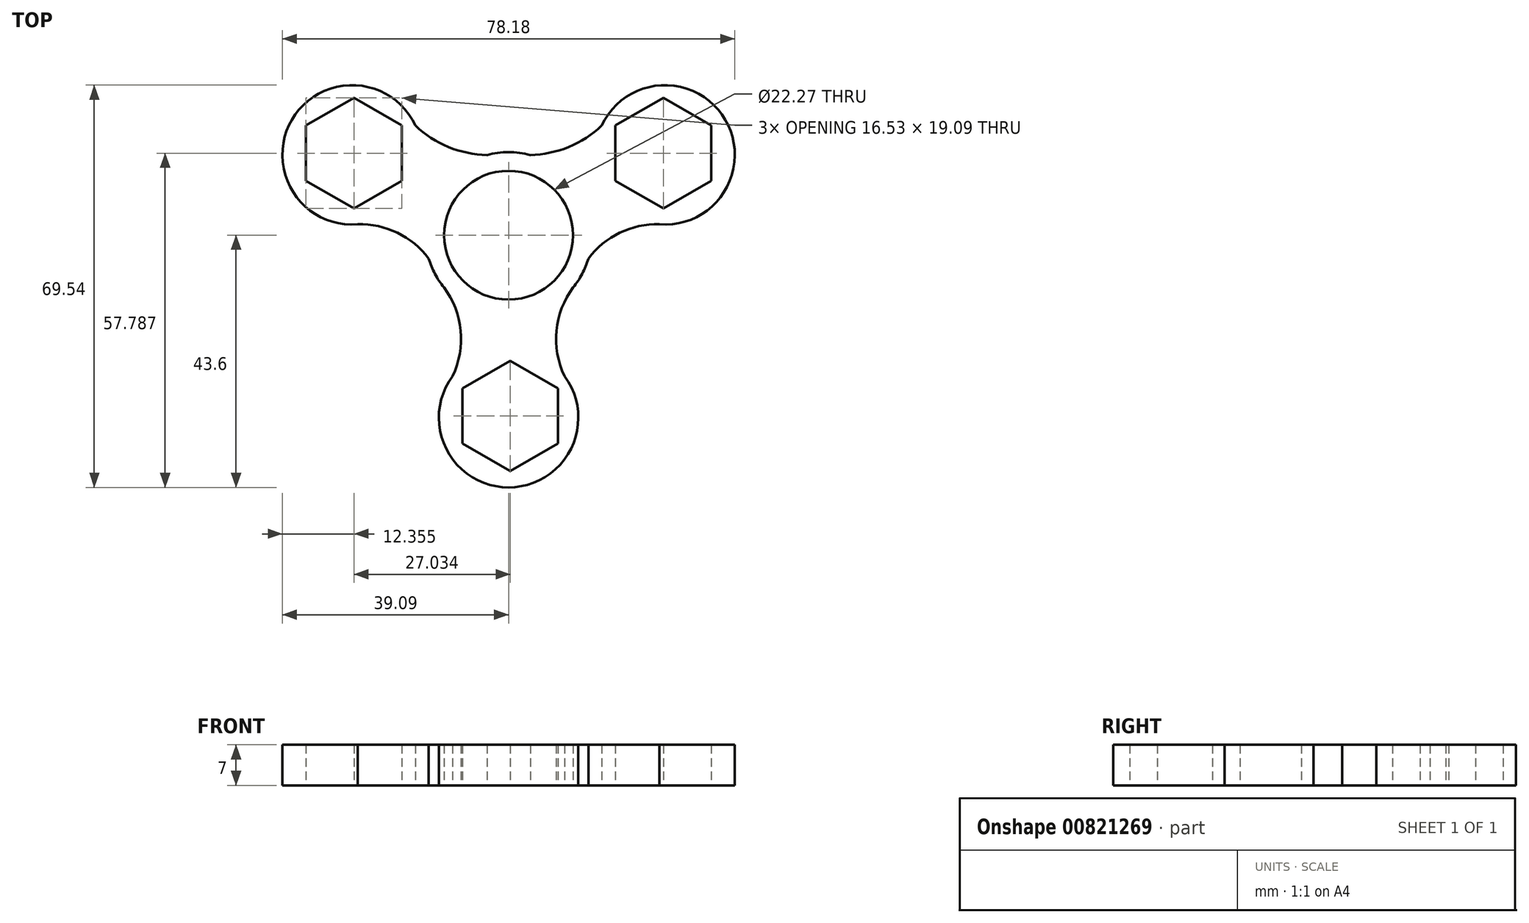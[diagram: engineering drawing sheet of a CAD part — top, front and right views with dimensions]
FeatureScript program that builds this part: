
annotation { "Feature Type Name" : "Feature", "Feature Type Description" : "" }
export const myFeature = defineFeature(function(context is Context, id is Id, definition is map)
    precondition{}
    {
        {
            var Q0;
            Q0=qCreatedBy(makeId("Top.planeOp"),FACE);
            var sketch = newSketch(context, id + "F0", { "sketchPlane" : qUnion([Q0])});
            skCircle(sketch, "E0", {"center": v(0, 0) * mm, "radius": 11.14 * mm});
            skCircle(sketch, "E1", {"center": v(0, 0) * mm, "radius": 14.37 * mm});
            skCircle(sketch, "E2", {"center": v(0, -31.54) * mm, "radius": 12.05 * mm});
            skLineSegment(sketch, "E3.0", {"start": v(8.56, -26.47) * mm, "end": v(8.56, -36.02) * mm});
            skLineSegment(sketch, "E3.1", {"start": v(8.56, -36.02) * mm, "end": v(0.3, -40.79) * mm});
            skLineSegment(sketch, "E3.2", {"start": v(0.3, -40.79) * mm, "end": v(-7.97, -36.02) * mm});
            skLineSegment(sketch, "E3.3", {"start": v(-7.97, -36.02) * mm, "end": v(-7.97, -26.47) * mm});
            skLineSegment(sketch, "E3.4", {"start": v(-7.97, -26.47) * mm, "end": v(0.3, -21.7) * mm});
            skLineSegment(sketch, "E3.5", {"start": v(0.3, -21.7) * mm, "end": v(8.56, -26.47) * mm});
            skCircle(sketch, "E4", {"center": v(-27.03, 13.89) * mm, "radius": 12.05 * mm});
            skLineSegment(sketch, "E5.0", {"start": v(-18.47, 18.96) * mm, "end": v(-18.47, 9.42) * mm});
            skLineSegment(sketch, "E5.1", {"start": v(-18.47, 9.42) * mm, "end": v(-26.74, 4.64) * mm});
            skLineSegment(sketch, "E5.2", {"start": v(-26.74, 4.64) * mm, "end": v(-35, 9.42) * mm});
            skLineSegment(sketch, "E5.3", {"start": v(-35, 9.42) * mm, "end": v(-35, 18.96) * mm});
            skLineSegment(sketch, "E5.4", {"start": v(-35, 18.96) * mm, "end": v(-26.74, 23.73) * mm});
            skLineSegment(sketch, "E5.5", {"start": v(-26.74, 23.73) * mm, "end": v(-18.47, 18.96) * mm});
            skLineSegment(sketch, "E6.MirrorCS", {"start": v(18.47, 18.96) * mm, "end": v(18.47, 9.42) * mm});
            skLineSegment(sketch, "E7.MirrorCS", {"start": v(35, 9.42) * mm, "end": v(35, 18.96) * mm});
            skLineSegment(sketch, "E8.MirrorCS", {"start": v(26.74, 23.73) * mm, "end": v(18.47, 18.96) * mm});
            skLineSegment(sketch, "E9.MirrorCS", {"start": v(35, 18.96) * mm, "end": v(26.74, 23.73) * mm});
            skLineSegment(sketch, "E10.MirrorCS", {"start": v(18.47, 9.42) * mm, "end": v(26.74, 4.64) * mm});
            skLineSegment(sketch, "E11.MirrorCS", {"start": v(26.74, 4.64) * mm, "end": v(35, 9.42) * mm});
            skCircle(sketch, "E12.MirrorC", {"center": v(27.03, 13.89) * mm, "radius": 12.05 * mm});
            skPoint(sketch, "E13", {"position": v(-11.12, -9.1) * mm});
            skPoint(sketch, "E14", {"position": v(11.48, -8.64) * mm});
            skPoint(sketch, "E15", {"position": v(0, 14.19) * mm});
            skPoint(sketch, "E15.positionSnap0", {"position": v(35, 14.19) * mm});
            skArc(sketch, "E16", {"start": v(-16.1, 18.96) * mm, "mid": v(-8.63, 14.63) * mm, "end": v(0, 14.19) * mm});
            skArc(sketch, "E17.MirrorCS", {"start": v(16.1, 18.96) * mm, "mid": v(8.63, 14.63) * mm, "end": v(0, 14.19) * mm});
            skArc(sketch, "E18", {"start": v(11.48, -8.64) * mm, "mid": v(8.2, -17.46) * mm, "end": v(10.93, -26.47) * mm});
            skArc(sketch, "E19.MirrorCS", {"start": v(-11.48, -8.64) * mm, "mid": v(-8.2, -17.46) * mm, "end": v(-10.93, -26.47) * mm});
            skArc(sketch, "E20", {"start": v(26.72, 1.84) * mm, "mid": v(17.25, -0.72) * mm, "end": v(11.48, -8.64) * mm});
            skArc(sketch, "E21.MirrorCS", {"start": v(-26.72, 1.84) * mm, "mid": v(-17.25, -0.72) * mm, "end": v(-11.48, -8.64) * mm});
            skSolve(sketch);
        }
        {
            var Q0;
            Q0 = qSketchRegion(id + "F0", true);
            extrude(context, id + "F1", {"entities" : qUnion([Q0]), "depth" : 7 * mm, "offsetDistance" : 25 * mm});
        }
    });
